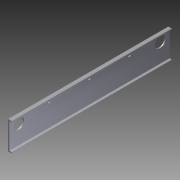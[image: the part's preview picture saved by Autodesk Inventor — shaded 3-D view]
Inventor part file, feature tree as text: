
AUTODESK INVENTOR PART (.ipt)
format: ipt  version: 2012 (Build 160160000, 160)  size: 108,032 bytes
history: native  units: in
note: dims shown in document units (in); Inventor stores cm internally (conversion verified against a paired STEP export)
features: extrude x2, sketch x2
ambient origin geometry x8: Origin, YZ Plane, XZ Plane, XY Plane, X Axis, Y Axis, Z Axis, Center Point
bodies: Solid1 (feature_tree)
feature tree (4):
  extrude  "Extrusion1"  Depth=0.125in
  extrude  "Extrusion2"  Depth=3.0in
  sketch  "Sketch1"  dims[d0=0.125in d2=0.125in]
  sketch  "Sketch2"  dims[d3=0.125in d4=3.0in d5=0.375in d6=17.125in d7=0.0in d8=1.125in d10=2.125in d11=1.0in d12=20.0in d13=0.0in d14=1.0in d15=2.125in d16=1.125in d17=0.25in d18=0.5in d19=8.5625in d20=4.2813in d21=4.2813in d22=0.25in d23=0.25in d24=17.125in]
